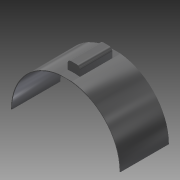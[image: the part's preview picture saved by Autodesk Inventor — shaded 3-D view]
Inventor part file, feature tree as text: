
AUTODESK INVENTOR PART (.ipt)
format: ipt  version: 2012 (Build 160160000, 160)  size: 104,448 bytes
history: native  units: in
note: dims shown in document units (in); Inventor stores cm internally (conversion verified against a paired STEP export)
features: extrude x2, sketch x1, fillet x1
ambient origin geometry x8: Origin, YZ Plane, XZ Plane, XY Plane, X Axis, Y Axis, Z Axis, Center Point
bodies: Solid1 (feature_tree)
feature tree (4):
  sketch  "Sketch1"  dims[d16=1.0in d18=0.23in d19=0.115in d20=0.17in d23=0.014in d24=1.014in d25=0.9in d26=0.0in d27=0.6in d28=0.0in d29=0.0625in]
  extrude  "Extrusion1"  Depth=0.23in
  extrude  "Extrusion2"  Depth=0.115in
  fillet  "Fillet1"  Radius=0.17in
